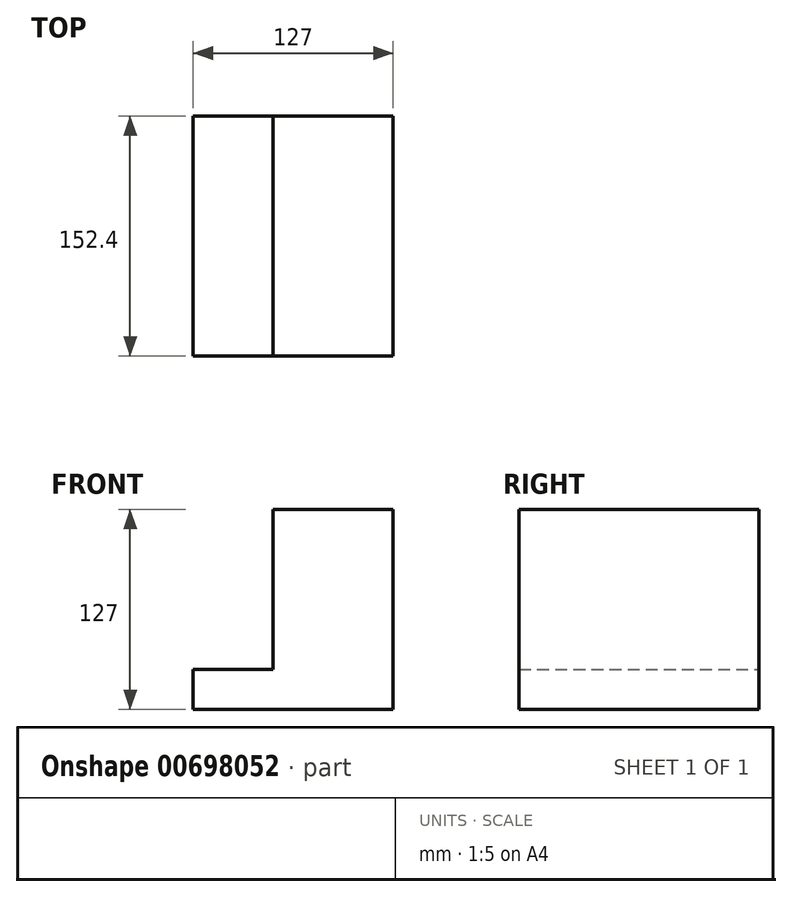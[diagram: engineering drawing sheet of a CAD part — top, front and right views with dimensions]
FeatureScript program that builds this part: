
annotation { "Feature Type Name" : "Feature", "Feature Type Description" : "" }
export const myFeature = defineFeature(function(context is Context, id is Id, definition is map)
    precondition{}
    {
        {
            var Q0;
            Q0=qCreatedBy(makeId("Front.planeOp"),FACE);
            var sketch = newSketch(context, id + "F0", { "sketchPlane" : qUnion([Q0])});
            skLineSegment(sketch, "E0", {"start": v(-123.65, -14.2) * mm, "end": v(3.35, -14.2) * mm});
            skLineSegment(sketch, "E1", {"start": v(3.35, -14.2) * mm, "end": v(3.35, 112.8) * mm});
            skLineSegment(sketch, "E2", {"start": v(3.35, 112.8) * mm, "end": v(-72.85, 112.8) * mm});
            skLineSegment(sketch, "E3", {"start": v(-72.85, 112.8) * mm, "end": v(-72.85, 11.2) * mm});
            skLineSegment(sketch, "E4", {"start": v(-72.85, 11.2) * mm, "end": v(-123.65, 11.2) * mm});
            skLineSegment(sketch, "E5", {"start": v(-123.65, 11.2) * mm, "end": v(-123.65, -14.2) * mm});
            skSolve(sketch);
        }
        {
            var Q0;
            Q0=makeQuery(id+"F0.imprint","IMPRINT",FACE,{"disambiguationData":[TD([[makeQuery(id+"F0.imprint","IMPRINT",EDGE,{"derivedFrom":sQuery(id+"F0.wireOp",EDGE,"E0")}),1.0]])]});
            extrude(context, id + "F1", {"entities" : qUnion([Q0]), "depth" : 152.4 * mm, "offsetDistance" : 25.4 * mm});
        }
    });
